# Revit family: F1AI_2803-2843-2606_OS265
name_source: partatom
category: Finestre
units: mm (PartAtom-declared; Revit-internal decimal feet)

## family parameters
Condiviso = No
Host = Muro
Numero OmniClass = 23.30.20.00
Punto di calcolo locali = No
Sempre verticale = Sì
Taglio con vuoti quando caricato = No
Titolo OmniClass = Windows

## types (4) — shared parameters
Altezza di default del davanzale = 800 mm
Chiusura muro = Per host
Costruzione analitica = <Nessuno>
Descrizione = Finestra 1 anta a battente
H_Max = 2900 mm
H_Min = 300 mm
L = 1000 mm  [stored 3.28084 ft]
L1 = 1000 mm  [stored 3.28084 ft]
L_Max = 1000 mm  [stored 3.28084 ft]
L_Min = 300 mm
L_fermavetro = 936 mm
L_vetro = 924 mm  [stored 3.0315 ft]
Maniglia_alta = 1050 mm  [stored 3.44488 ft]
Maniglia_media = 500 mm  [stored 1.64042 ft]
Modello = OS2 65
Nota tecnica = https://www.seccosistemi.com
Produttore = Secco Sistemi Spa
n2_cerniere = 2
n2_scarichi = 2
n3_cerniere = 3
n3_scarichi = 3
n4_cerniere = 4
numero_scarichi = 3

## per-type parameters (varying)
| type | Altezza | H | H1 | H_fermavetro | H_man | H_maniglia | H_vetro | Larghezza | MATERIALE | Maniglia_bassa | URL | WARNING | numero_cerniere |
| Ottone | 1000 mm  [stored 3.28084 ft] | 1000 mm  [stored 3.28084 ft] | 1000 mm  [stored 3.28084 ft] | 936 mm | 500 mm  [stored 1.64042 ft] | 500 mm  [stored 1.64042 ft] | 924 mm  [stored 3.0315 ft] | 1000 mm  [stored 3.28084 ft] | Ottone | 500 mm  [stored 1.64042 ft] |  | No | 2 |
| Acciaio zincato | 1500 mm  [stored 4.92126 ft] | 1500 mm  [stored 4.92126 ft] | 1500 mm  [stored 4.92126 ft] | 1436 mm | 500 mm  [stored 1.64042 ft] | 500 mm  [stored 1.64042 ft] | 1424 mm | 1500 mm  [stored 4.92126 ft] | Acciaio | 750 mm |  | Sì | 3 |
| Acciaio inox | 1500 mm  [stored 4.92126 ft] | 1500 mm  [stored 4.92126 ft] | 1500 mm  [stored 4.92126 ft] | 1436 mm | 500 mm  [stored 1.64042 ft] | 500 mm  [stored 1.64042 ft] | 1424 mm | 1500 mm  [stored 4.92126 ft] | Acciaio inox, spazzolato | 750 mm |  | Sì | 3 |
| Acciaio corten | 800 mm | 800 mm | 800 mm | 736 mm | 400 mm  [stored 1.31234 ft] | 400 mm  [stored 1.31234 ft] | 724 mm | 1000 mm  [stored 3.28084 ft] | Acciaio corten | 400 mm  [stored 1.31234 ft] | https://www.seccosistemi.com | No | 2 |

note: [stored X ft] marks values corroborated as IEEE doubles in the binary element streams (Revit-internal decimal feet)
